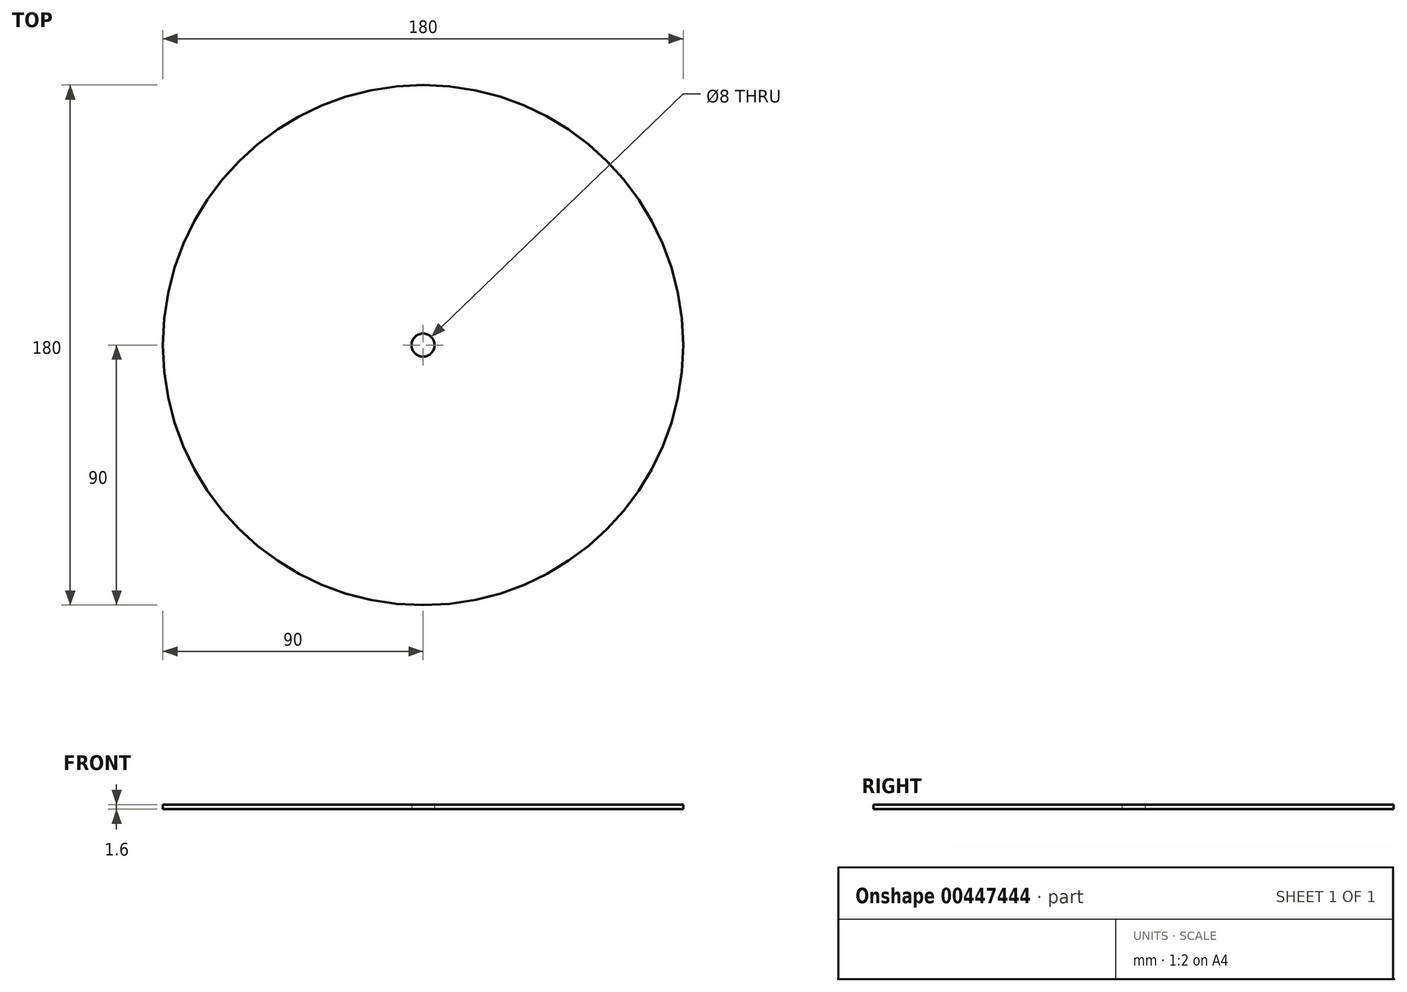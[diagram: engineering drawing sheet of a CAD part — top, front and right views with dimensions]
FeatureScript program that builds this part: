
annotation { "Feature Type Name" : "Feature", "Feature Type Description" : "" }
export const myFeature = defineFeature(function(context is Context, id is Id, definition is map)
    precondition{}
    {
        {
            var Q0;
            Q0=qCreatedBy(makeId("Top.planeOp"),FACE);
            var sketch = newSketch(context, id + "F0", { "sketchPlane" : qUnion([Q0])});
            skCircle(sketch, "E0", {"center": v(0, 0) * mm, "radius": 90 * mm});
            skCircle(sketch, "E1", {"center": v(0, 0) * mm, "radius": 4 * mm});
            skSolve(sketch);
        }
        {
            var Q0;
            Q0 = qSketchRegion(id + "F0", true);
            extrude(context, id + "F1", {"entities" : qUnion([Q0]), "depth" : 1.6 * mm});
        }
    });
